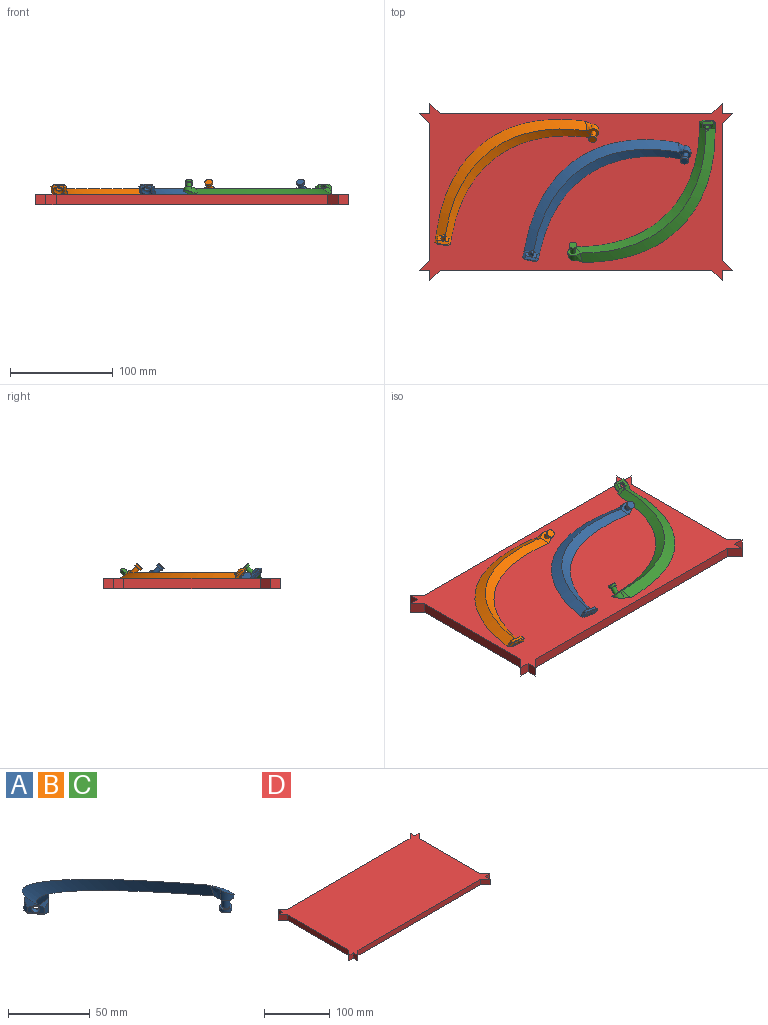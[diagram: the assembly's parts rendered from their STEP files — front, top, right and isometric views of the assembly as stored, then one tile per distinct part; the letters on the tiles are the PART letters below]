
ASSEMBLY  parts=4 mates=3
PART A: 41 faces, bbox 52.2x175.5x102 mm
  f0: plane 5.18x4.18mm, normal (0.79,0.61,0.05), area 6mm2, adj f9,f23,f27
  f1: plane 5.11x4.38mm, normal (0.79,0.61,0.05), area 6mm2, adj f9,f23,f33
  f2: plane 8.42x6.23mm, normal (-0.82,-0.41,0.4), area 27.8mm2, adj f5,f19,f25,f33,f39,f40
  f3: plane 5.85x5.64mm, normal (-0.52,-0.76,0.39), area 17.3mm2, adj f6,f18,f25,f27,f28,f31
  f4: cylinder r=180mm len=150.82mm, axis (1,0,0), area 1766.1mm2, adj f5,f6,f9,f11,f25,f26,f27
  f5: bspline ~160.22x93.24mm, area 2224.1mm2, adj f2,f4,f9,f13,f25,f26,f33
  f6: plane 5.86x3.44mm, normal (-0.58,-0.46,0.67), area 0.1mm2, adj f3,f4,f25,f27
  f7: cylinder r=2.5mm len=6.12mm, axis (0.79,0.61,0.05), area 55.5mm2, adj f23,f25
  f8: plane 3.12x1.11mm, normal (0.79,0.61,0.05), area 1mm2, adj f23,f27,f30
  f9: plane 160.23x89.78mm, normal (0.54,0.41,0.74), area 3428.4mm2, adj f0,f1,f4,f5,f10,f27,f33
  f10: plane 15.29x11.53mm, normal (0.59,0,0.81), area 122mm2, adj f9,f11,f12,f13
  f11: plane 10x10mm, normal (0,0,-1), area 69.6mm2, adj f4,f10,f12,f13,f14
  f12: cylinder r=5mm len=10mm, axis (0,0,-1), area 57.1mm2, adj f10,f11,f13
  f13: bspline ~10x5mm, area 47.1mm2, adj f5,f10,f11,f12
  f14: cylinder r=2.5mm len=7.5mm, axis (0,0,1), area 117.8mm2, adj f11,f15
  f15: plane 7.5x7.5mm, normal (0,0,1), area 24.5mm2, adj f14,f16
  f16: cylinder r=3.75mm len=7.5mm, axis (0,0,1), area 58.9mm2, adj f15,f17
  f17: plane 7.5x7.5mm, normal (0,0,-1), area 44.2mm2, adj f16
  f18: plane 4.03x0.75mm, normal (0.62,-0.79,-0.02), area 2.4mm2, adj f3,f21,f27,f28
  f19: plane 4.03x0.75mm, normal (-0.61,0.79,0.01), area 2.4mm2, adj f2,f22,f33,f40
  f20: plane 3.13x0.99mm, normal (0.79,0.61,0.05), area 1mm2, adj f23,f30,f33
  f21: plane 6.24x0.86mm, normal (0.61,-0.79,-0.01), area 5.2mm2, adj f18,f27,f31,f32
  f22: plane 6.25x0.87mm, normal (-0.61,0.79,0.01), area 5.2mm2, adj f19,f33,f37,f39
  f23: sphere r=7.5mm, area 73mm2, adj f0,f1,f7,f8,f20,f27,f30,f33
  f24: plane 8.91x7.23mm, normal (0.03,0.04,-1), area 9.6mm2, adj f30,f32,f36,f37
  f25: plane 8.54x8.17mm, normal (-0.79,-0.61,-0.05), area 42mm2, adj f2,f3,f4,f5,f6,f7,f26,f31
  f26: cylinder r=5mm len=3.7mm, axis (0.79,0.61,0.05), area 3.1mm2, adj f4,f5,f25
  f27: plane 10.61x3.53mm, normal (0.99,-0.12,0.02), area 29.4mm2, adj f0,f3,f4,f6,f8,f9,f18,f21
  f28: plane 2.28x2.27mm, normal (-0.12,-0.99,-0.05), area 2.5mm2, adj f3,f18,f31
  f29: plane 3.09x2.3mm, normal (0.83,-0.08,-0.56), area 4.2mm2, adj f27,f30,f32
  f30: plane 9.62x8.19mm, normal (0.58,0.46,-0.67), area 24.8mm2, adj f8,f20,f23,f24,f29,f35
  f31: plane 5.38x3.22mm, normal (-0.12,-0.99,-0.04), area 16.2mm2, adj f3,f21,f25,f28,f34
  f32: plane 2.38x2.21mm, normal (0.45,-0.53,-0.72), area 2.8mm2, adj f21,f24,f29,f34
  f33: plane 10.63x3.45mm, normal (0.12,0.99,0.04), area 29.3mm2, adj f1,f2,f5,f9,f19,f20,f22,f23
  f34: plane 3.09x2.17mm, normal (-0.08,-0.79,-0.61), area 4.2mm2, adj f31,f32,f36
  f35: plane 3.09x2.3mm, normal (0.12,0.83,-0.54), area 4.2mm2, adj f30,f33,f37
  f36: plane 9.8x8.31mm, normal (-0.54,-0.41,-0.74), area 33mm2, adj f24,f25,f34,f38
  f37: plane 2.27x2.2mm, normal (-0.41,0.59,-0.7), area 2.8mm2, adj f22,f24,f35,f38
  f38: plane 3.09x2.23mm, normal (-0.79,0.12,-0.6), area 4.2mm2, adj f36,f37,f39
  f39: plane 5.44x3.26mm, normal (-0.99,0.12,-0.02), area 15.8mm2, adj f2,f22,f25,f38,f40
  f40: plane 2.31x1.98mm, normal (-0.99,0.13,-0.03), area 2.2mm2, adj f2,f19,f39
PART B: same geometry as A
PART C: same geometry as A
PART D: 22 faces, bbox 304.5x172.4x10 mm
  f0: plane 10x10mm, normal (0,-1,0), area 100mm2, adj f1,f19,f20,f21
  f1: plane 10x10mm, normal (-1,0,0), area 100mm2, adj f0,f2,f20,f21
  f2: plane 10x10mm, normal (0.71,-0.71,0), area 141.4mm2, adj f1,f3,f20,f21
  f3: plane 264.48x10mm, normal (0,-1,0), area 2644.8mm2, adj f2,f4,f20,f21
  f4: plane 10x10mm, normal (-0.71,-0.71,0), area 141.4mm2, adj f3,f5,f20,f21
  f5: plane 10x10mm, normal (1,0,0), area 100mm2, adj f4,f6,f20,f21
  f6: plane 10x10mm, normal (0,-1,0), area 100mm2, adj f5,f7,f20,f21
  f7: plane 10x10mm, normal (0.71,0.71,0), area 141.4mm2, adj f6,f8,f20,f21
  f8: plane 132.4x10mm, normal (1,0,0), area 1324mm2, adj f7,f9,f20,f21
  f9: plane 10x10mm, normal (0.71,-0.71,0), area 141.4mm2, adj f8,f10,f20,f21
  f10: plane 10x10mm, normal (0,1,0), area 100mm2, adj f9,f11,f20,f21
  f11: plane 10x10mm, normal (1,0,0), area 100mm2, adj f10,f12,f20,f21
  f12: plane 10x10mm, normal (-0.71,0.71,0), area 141.4mm2, adj f11,f13,f20,f21
  f13: plane 264.48x10mm, normal (0,1,0), area 2644.8mm2, adj f12,f14,f20,f21
  f14: plane 10x10mm, normal (0.71,0.71,0), area 141.4mm2, adj f13,f15,f20,f21
  f15: plane 10x10mm, normal (-1,0,0), area 100mm2, adj f14,f16,f20,f21
  f16: plane 10x10mm, normal (0,1,0), area 100mm2, adj f15,f17,f20,f21
  f17: plane 10x10mm, normal (-0.71,-0.71,0), area 141.4mm2, adj f16,f18,f20,f21
  f18: plane 132.4x10mm, normal (-1,0,0), area 1324mm2, adj f17,f19,f20,f21
  f19: plane 10x10mm, normal (-0.71,0.71,0), area 141.4mm2, adj f0,f18,f20,f21
  f20: plane 304.48x172.4mm, normal (0,0,1), area 43754.8mm2, adj f0,f1,f2,f3,f4,f5,f6,f7
  f21: plane 304.48x172.4mm, normal (0,0,-1), area 43754.8mm2, adj f0,f1,f2,f3,f4,f5,f6,f7
PLACE A rot(axis=(-0.84,0.52,0.14),140.7deg) t=(98.03,-24.01,76.31)mm
PLACE B rot(axis=(-0.85,0.5,0.15),141deg) t=(10.83,-3.35,76.31)mm
PLACE C rot(axis=(0.43,0.84,-0.33),161.7deg) t=(0.08,0.91,76.31)mm
PLACE D t=(2.46,-1.08,-167.35)mm fixed
MATE planar A.f9 <-> D.f20  axis (0,0,-1) through (15.85,11.4,5.05)mm
MATE planar B.f9 <-> D.f20  axis (0,0,-1) through (-72.65,28.88,5.05)mm
MATE planar C.f9 <-> D.f20  axis (0,0,-1) through (87.15,-19.69,5.05)mm
